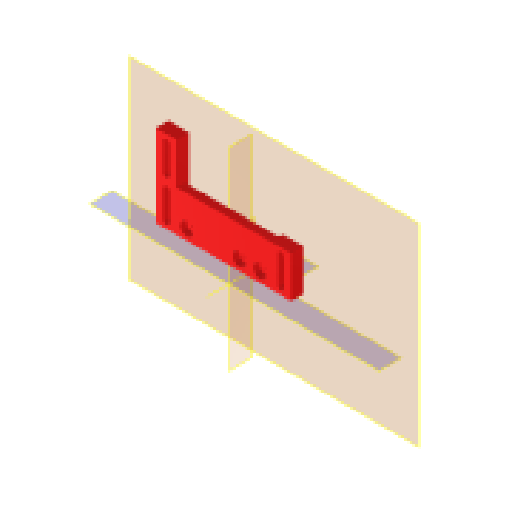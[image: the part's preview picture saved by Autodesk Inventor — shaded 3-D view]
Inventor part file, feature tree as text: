
AUTODESK INVENTOR PART (.ipt)
format: ipt  version: 2025.3 (Build 293356000, 356)  size: 259,072 bytes
history: native  units: mm
features: other x14, reference x11, plane x9, extrude x6, sketch x6, projected_geometry x3, hole x1
ambient origin geometry x8: Origin, YZ Plane, XZ Plane, XY Plane, X Axis, Y Axis, Z Axis, Center Point
bodies: Volumenkörper1 (feature_tree)
feature tree (50):
  plane  "Arbeitsebene1"
  plane  "Arbeitsebene2"
  extrude  "Extrusion1"  Depth=6.0mm
  hole  "Bohrung1"  [1 undecoded]
  sketch  "Skizze3"  dims[d2=2.9mm d3=6.0mm d4=6.5mm d5=3.0mm d6=90.0deg d7=8.0mm d8=20.594885mm d9=38.0mm]
  other  "Arbeitspunkt1"
  plane  "Arbeitsebene4"
  plane  "Arbeitsebene5"
  extrude  "Extrusion2"  Depth=10.0mm
  plane  "Arbeitsebene3"
  other  "Arbeitsachse1"
  plane  "Arbeitsebene8"
  extrude  "Extrusion5"  Depth=10.0mm
  extrude  "Extrusion6"  Depth=10.0mm
  extrude  "Extrusion7"  Depth=10.0mm
  sketch  "Sketch11"  dims[d31=10.0mm d32=10.0mm d33=10.0mm d34=6.5mm d35=3.2mm d36=6.5mm d37=3.2mm d47=11.8mm d49=20.0mm d50=6.5mm d51=3.2mm d54=0.1mm d55=12.5mm d56=0.0mm d57=12.0mm d58=0.0mm d59=0.0mm d60=10.0mm d61=0.0mm d62=10.0mm d63=0.0mm]
  plane  "Work Plane9"
  extrude  "Extrusion8"  Depth=10.0mm
  reference  "Referenz1"
  reference  "Referenz3"
  reference  "Referenz4"
  sketch  "Skizze2"  dims[d0=10.0mm d1=0.0mm]
  reference  "Referenz5"
  reference  "Referenz6"
  reference  "Referenz7"
  projected_geometry  "Projizierte Kontur1"
  reference  "Referenz8"
  reference  "Referenz9"
  plane  "Arbeitsebene6"
  plane  "Arbeitsebene7"
  sketch  "Skizze8"  dims[d10=10.0mm d11=10.0mm]
  reference  "Referenz18"
  sketch  "Skizze9"  dims[d12=10.0mm d13=10.0mm]
  projected_geometry  "Projizierte Kontur3"
  sketch  "Sketch10"  dims[d14=6.0mm d15=0.0mm d30=10.0mm]
  reference  "Reference19"
  reference  "Reference20"
  projected_geometry  "Projected Loop4"
  other  "Assemlby_Scanner_v1.iam"
  other  "00_CCTV_lens_M12_25mm_5mp:1"
  other  "Assemlby_lightsheet_generator_passive_v2.iam"
  other  "30_Lightsheet_generator_passive_lid_v0:1"
  other  "00_Thorlabs_LJ1878L1-A-Step:1"
  other  "<userpath>\Documents\HoLiSheet\INVENTOR\Assemlby_lightsheet_generator_passive_v2.iam"
  other  "30_Lightsheet_generator_singlegalvo_1:1"
  other  "30_Scanlens_Laseradaper_v1:1"
  other  "Assembly_Guinardia_V2.iam"
  other  "10_Wellplate_base_v2:1"
  other  "Assembly_Guinardia_V4.iam"
  other  "10_Wellplate_base_v3:1"
note: 1 required parameter value undecoded (feature->parameter linkage not recoverable at this tier; creation-order binding heuristic only, values carry confidence <= 0.55)
